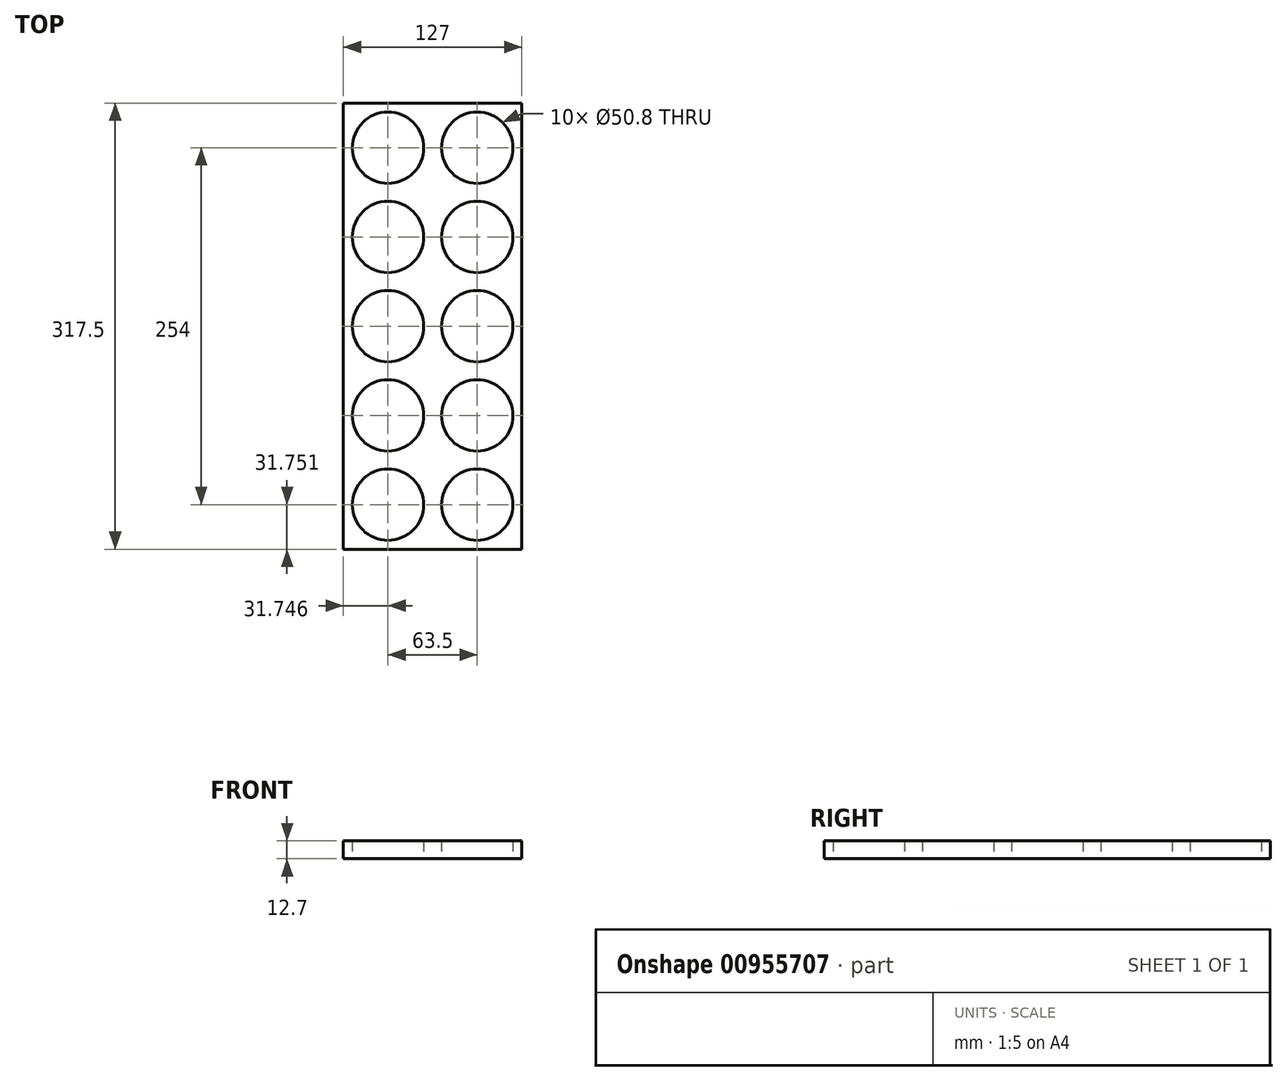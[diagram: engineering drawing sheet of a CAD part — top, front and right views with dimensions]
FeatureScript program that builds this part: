
annotation { "Feature Type Name" : "Feature", "Feature Type Description" : "" }
export const myFeature = defineFeature(function(context is Context, id is Id, definition is map)
    precondition{}
    {
        {
            var Q0;
            Q0=qCreatedBy(makeId("Top.planeOp"),FACE);
            var sketch = newSketch(context, id + "F0", { "sketchPlane" : qUnion([Q0])});
            skLineSegment(sketch, "E0.bottom", {"start": v(-74.58, 217.06) * mm, "end": v(52.42, 217.06) * mm});
            skLineSegment(sketch, "E0.top", {"start": v(-74.58, -100.44) * mm, "end": v(52.42, -100.44) * mm});
            skLineSegment(sketch, "E0.left", {"start": v(-74.58, 217.06) * mm, "end": v(-74.58, -100.44) * mm});
            skLineSegment(sketch, "E0.right", {"start": v(52.42, 217.06) * mm, "end": v(52.42, -100.44) * mm});
            skSolve(sketch);
        }
        {
            var Q0;
            Q0=makeQuery(id+"F0.imprint","IMPRINT",FACE,{"disambiguationData":[TD([[makeQuery(id+"F0.imprint","IMPRINT",EDGE,{"derivedFrom":sQuery(id+"F0.wireOp",EDGE,"E0.bottom")}),-1.0]])]});
            var sketch = newSketch(context, id + "F1", { "sketchPlane" : qUnion([Q0])});
            skLineSegment(sketch, "E1", {"start": v(-42.83, 220.59) * mm, "end": v(-42.83, -103.96) * mm, "construction": true});
            skLineSegment(sketch, "E2", {"start": v(20.67, 219.87) * mm, "end": v(20.67, -103.24) * mm, "construction": true});
            skLineSegment(sketch, "E3", {"start": v(-74.93, -68.69) * mm, "end": v(52.16, -68.69) * mm, "construction": true});
            skLineSegment(sketch, "E4", {"start": v(-74.15, -5.19) * mm, "end": v(52.94, -5.19) * mm, "construction": true});
            skLineSegment(sketch, "E5", {"start": v(-75.32, 58.31) * mm, "end": v(52.16, 58.31) * mm, "construction": true});
            skLineSegment(sketch, "E6", {"start": v(-74.2, 121.81) * mm, "end": v(56.25, 121.81) * mm, "construction": true});
            skLineSegment(sketch, "E7", {"start": v(-75.02, 185.31) * mm, "end": v(52.92, 185.31) * mm, "construction": true});
            skCircle(sketch, "E8", {"center": v(-42.83, 185.31) * mm, "radius": 25.4 * mm});
            skCircle(sketch, "E9", {"center": v(20.67, 185.31) * mm, "radius": 25.4 * mm});
            skCircle(sketch, "E10", {"center": v(-42.83, 121.81) * mm, "radius": 25.4 * mm});
            skCircle(sketch, "E11", {"center": v(20.67, 121.81) * mm, "radius": 25.4 * mm});
            skCircle(sketch, "E12", {"center": v(-42.83, 58.31) * mm, "radius": 25.4 * mm});
            skCircle(sketch, "E13", {"center": v(20.67, 58.31) * mm, "radius": 25.4 * mm});
            skCircle(sketch, "E14", {"center": v(-42.83, -5.19) * mm, "radius": 25.4 * mm});
            skCircle(sketch, "E15", {"center": v(20.67, -5.19) * mm, "radius": 25.4 * mm});
            skCircle(sketch, "E16", {"center": v(-42.83, -68.69) * mm, "radius": 25.4 * mm});
            skCircle(sketch, "E17", {"center": v(20.67, -68.69) * mm, "radius": 25.4 * mm});
            skSolve(sketch);
        }
        {
            var Q0;
            Q0 = qSketchRegion(id + "F0", true);
            extrude(context, id + "F2", {"entities" : qUnion([Q0]), "depth" : 12.7 * mm, "offsetDistance" : 25.4 * mm});
        }
        {
            var Q0;
            Q0 = qSketchRegion(id + "F1", true);
            extrude(context, id + "F3", {"entities" : qUnion([Q0]), "operationType" : NewBodyOperationType.REMOVE, "endBound" : BoundingType.UP_TO_NEXT, "depth" : 90.42 * mm, "offsetDistance" : 25.4 * mm});
        }
    });
